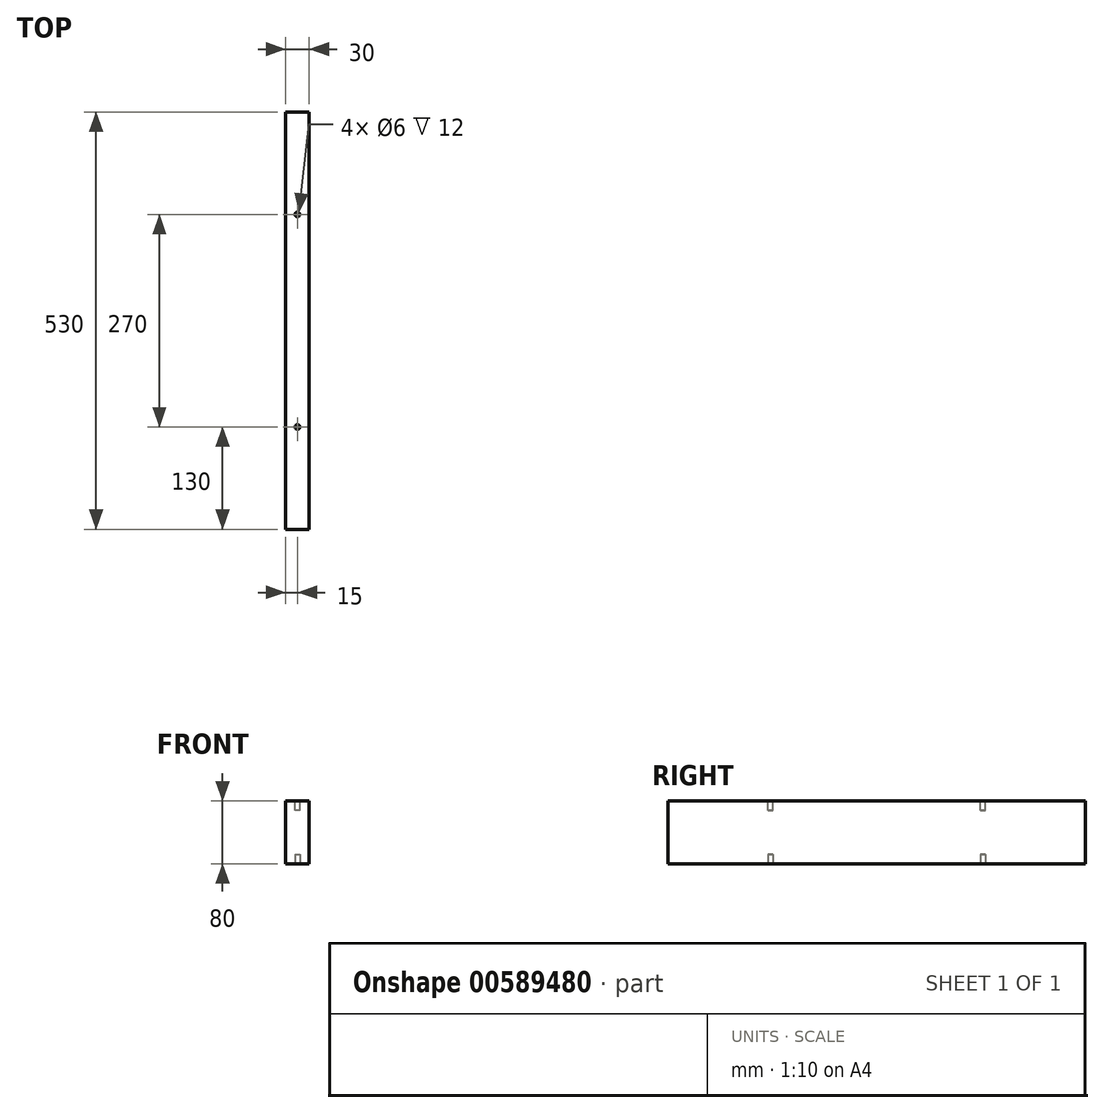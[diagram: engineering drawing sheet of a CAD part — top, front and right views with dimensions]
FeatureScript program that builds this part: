
annotation { "Feature Type Name" : "Feature", "Feature Type Description" : "" }
export const myFeature = defineFeature(function(context is Context, id is Id, definition is map)
    precondition{}
    {
        {
            var Q0;
            Q0=qCreatedBy(makeId("Right.planeOp"),FACE);
            var sketch = newSketch(context, id + "F0", { "sketchPlane" : qUnion([Q0])});
            skLineSegment(sketch, "E0.bottom", {"start": v(0, 0) * mm, "end": v(530, 0) * mm});
            skLineSegment(sketch, "E0.top", {"start": v(0, 80) * mm, "end": v(530, 80) * mm});
            skLineSegment(sketch, "E0.left", {"start": v(0, 0) * mm, "end": v(0, 80) * mm});
            skLineSegment(sketch, "E0.right", {"start": v(530, 0) * mm, "end": v(530, 80) * mm});
            skSolve(sketch);
        }
        {
            var Q0;
            Q0=makeQuery(id+"F0.imprint","IMPRINT",FACE,{"disambiguationData":[TD([[makeQuery(id+"F0.imprint","IMPRINT",EDGE,{"derivedFrom":sQuery(id+"F0.wireOp",EDGE,"E0.bottom")}),1.0]])]});
            extrude(context, id + "F1", {"entities" : qUnion([Q0]), "depth" : 30 * mm, "offsetDistance" : 25 * mm});
        }
        {
            var Q0;
            Q0=makeQuery(id+"F1.opExtrude","SWEPT_FACE",FACE,{"disambiguationData":[OSD([sQuery(id+"F0.wireOp",EDGE,"E0.bottom")])]});
            var sketch = newSketch(context, id + "F2", { "sketchPlane" : qUnion([Q0])});
            skCircle(sketch, "E1", {"center": v(15, -130) * mm, "radius": 3 * mm});
            skPoint(sketch, "E1.centerSnap0", {"position": v(15, 0) * mm});
            skSolve(sketch);
        }
        {
            var Q0;
            Q0=makeQuery(id+"F2.imprint","IMPRINT",FACE,{"disambiguationData":[TD([[makeQuery(id+"F2.imprint","IMPRINT",EDGE,{"derivedFrom":sQuery(id+"F2.wireOp",EDGE,"E1")}),1.0]])]});
            extrude(context, id + "F3", {"entities" : qUnion([Q0]), "operationType" : NewBodyOperationType.REMOVE, "oppositeDirection" : true, "depth" : 12 * mm, "offsetDistance" : 25 * mm});
        }
        {
            var Q0;
            Q0=makeQuery(id+"F1.opExtrude","SWEPT_FACE",FACE,{"disambiguationData":[OSD([sQuery(id+"F0.wireOp",EDGE,"E0.top")])]});
            var sketch = newSketch(context, id + "F4", { "sketchPlane" : qUnion([Q0])});
            skCircle(sketch, "E2.0", {"center": v(15, 130) * mm, "radius": 3 * mm});
            skSolve(sketch);
        }
        {
            var Q0;
            Q0=makeQuery(id+"F4.imprint","IMPRINT",FACE,{"disambiguationData":[TD([[makeQuery(id+"F4.imprint","IMPRINT",EDGE,{"derivedFrom":sQuery(id+"F4.wireOp",EDGE,"E2.0")}),1.0]])]});
            extrude(context, id + "F5", {"entities" : qUnion([Q0]), "operationType" : NewBodyOperationType.REMOVE, "oppositeDirection" : true, "depth" : 12 * mm, "offsetDistance" : 25 * mm});
        }
        {
            var Q0;
            Q0=makeQuery(id+"F1.opExtrude","SWEPT_FACE",FACE,{"disambiguationData":[OSD([sQuery(id+"F0.wireOp",EDGE,"E0.bottom")])]});
            var sketch = newSketch(context, id + "F6", { "sketchPlane" : qUnion([Q0])});
            skCircle(sketch, "E3", {"center": v(15, -400) * mm, "radius": 3 * mm});
            skPoint(sketch, "E3.centerSnap0", {"position": v(15, -530) * mm});
            skSolve(sketch);
        }
        {
            var Q0;
            Q0=makeQuery(id+"F6.imprint","IMPRINT",FACE,{"disambiguationData":[TD([[makeQuery(id+"F6.imprint","IMPRINT",EDGE,{"derivedFrom":sQuery(id+"F6.wireOp",EDGE,"E3")}),1.0]])]});
            extrude(context, id + "F7", {"entities" : qUnion([Q0]), "operationType" : NewBodyOperationType.REMOVE, "oppositeDirection" : true, "depth" : 12 * mm, "offsetDistance" : 25 * mm});
        }
        {
            var Q0;
            Q0=makeQuery(id+"F1.opExtrude","SWEPT_FACE",FACE,{"disambiguationData":[OSD([sQuery(id+"F0.wireOp",EDGE,"E0.top")])]});
            var sketch = newSketch(context, id + "F8", { "sketchPlane" : qUnion([Q0])});
            skCircle(sketch, "E4.0", {"center": v(15, 400) * mm, "radius": 3 * mm});
            skSolve(sketch);
        }
        {
            var Q0;
            Q0=makeQuery(id+"F8.imprint","IMPRINT",FACE,{"disambiguationData":[TD([[makeQuery(id+"F8.imprint","IMPRINT",EDGE,{"derivedFrom":sQuery(id+"F8.wireOp",EDGE,"E4.0")}),1.0]])]});
            extrude(context, id + "F9", {"entities" : qUnion([Q0]), "operationType" : NewBodyOperationType.REMOVE, "oppositeDirection" : true, "depth" : 12 * mm, "offsetDistance" : 25 * mm});
        }
    });
